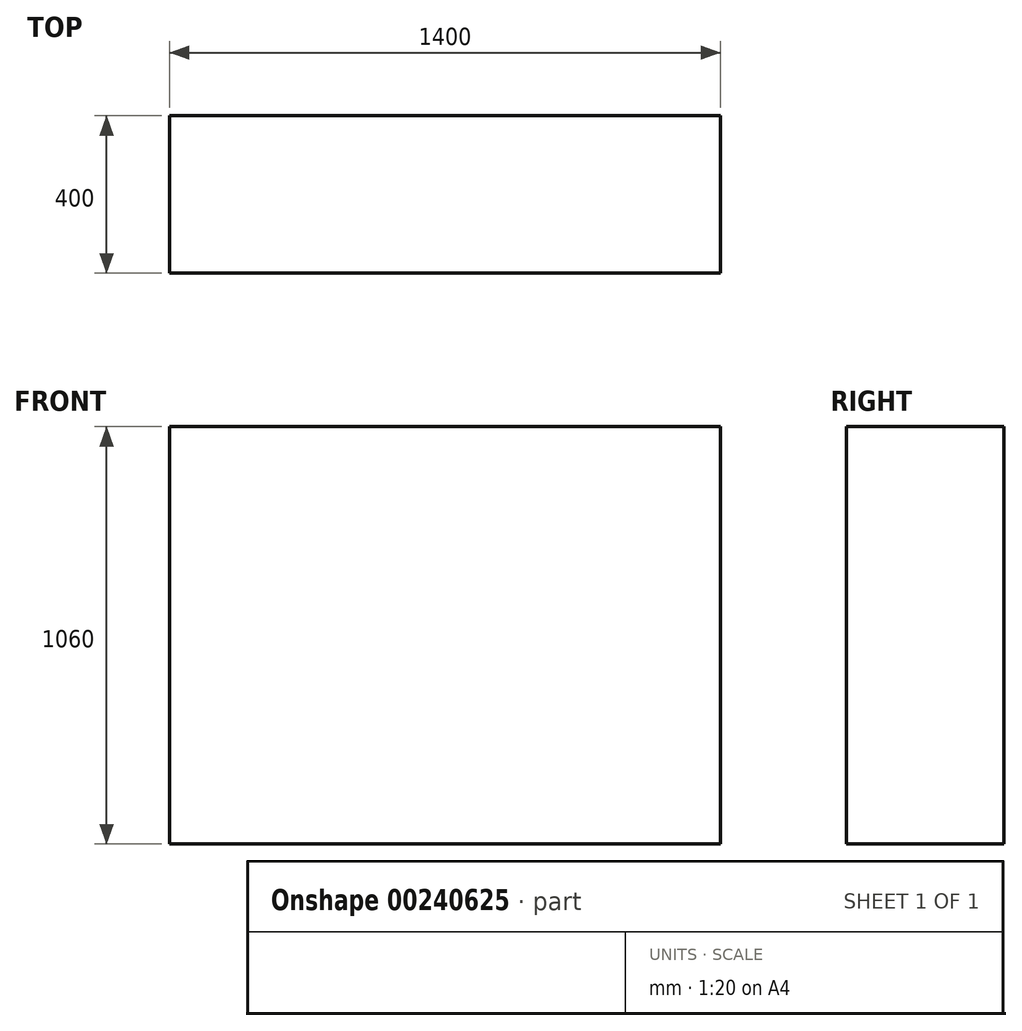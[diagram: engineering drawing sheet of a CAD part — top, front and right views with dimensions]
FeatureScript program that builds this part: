
annotation { "Feature Type Name" : "Feature", "Feature Type Description" : "" }
export const myFeature = defineFeature(function(context is Context, id is Id, definition is map)
    precondition{}
    {
        {
            var Q0;
            Q0=qCreatedBy(makeId("Front.planeOp"),FACE);
            var sketch = newSketch(context, id + "F0", { "sketchPlane" : qUnion([Q0])});
            skLineSegment(sketch, "E0.bottom", {"start": v(-1343.55, 989.98) * mm, "end": v(56.45, 989.98) * mm});
            skLineSegment(sketch, "E0.top", {"start": v(-1343.55, -70.02) * mm, "end": v(56.45, -70.02) * mm});
            skLineSegment(sketch, "E0.left", {"start": v(-1343.55, 989.98) * mm, "end": v(-1343.55, -70.02) * mm});
            skLineSegment(sketch, "E0.right", {"start": v(56.45, 989.98) * mm, "end": v(56.45, -70.02) * mm});
            skSolve(sketch);
        }
        {
            var Q0;
            Q0=makeQuery(id+"F0.imprint","IMPRINT",FACE,{"disambiguationData":[TD([[makeQuery(id+"F0.imprint","IMPRINT",EDGE,{"derivedFrom":sQuery(id+"F0.wireOp",EDGE,"E0.bottom")}),-1.0]])]});
            extrude(context, id + "F1", {"entities" : qUnion([Q0]), "depth" : 400 * mm});
        }
    });
